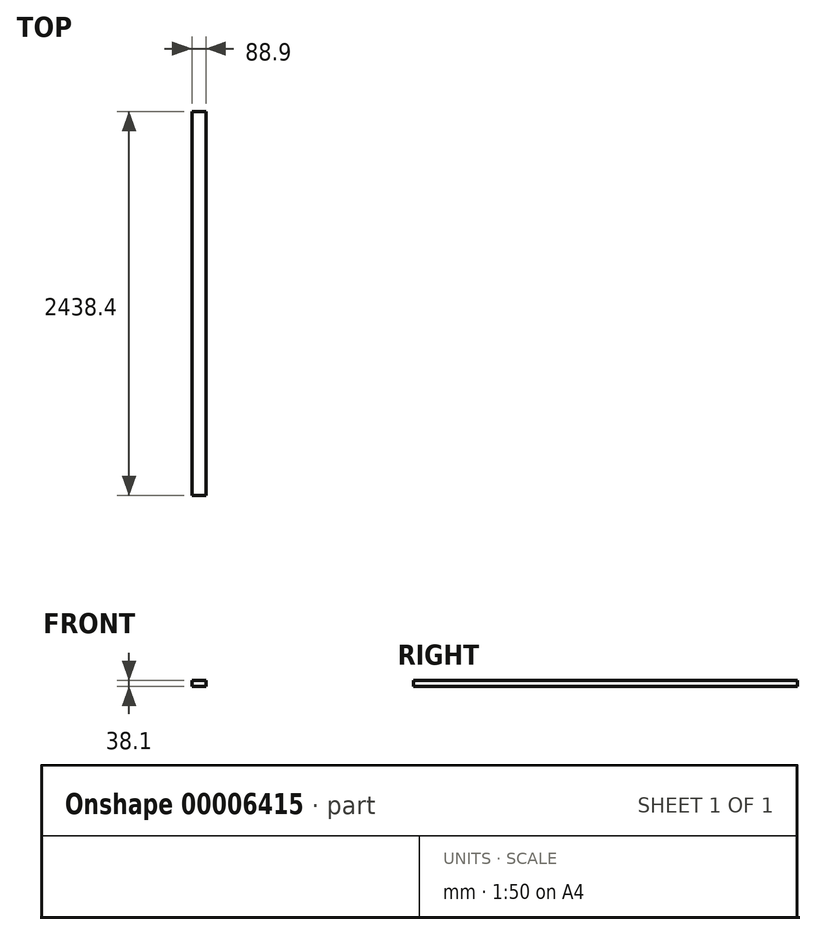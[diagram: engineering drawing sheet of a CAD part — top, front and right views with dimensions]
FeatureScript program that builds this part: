
annotation { "Feature Type Name" : "Feature", "Feature Type Description" : "" }
export const myFeature = defineFeature(function(context is Context, id is Id, definition is map)
    precondition{}
    {
        {
            var Q0;
            Q0=qCreatedBy(makeId("Front.planeOp"),FACE);
            var sketch = newSketch(context, id + "F0", { "sketchPlane" : qUnion([Q0])});
            skLineSegment(sketch, "E0.rect.bottom", {"start": v(44.45, -19.05) * mm, "end": v(-44.45, -19.05) * mm});
            skLineSegment(sketch, "E0.rect.top", {"start": v(44.45, 19.05) * mm, "end": v(-44.45, 19.05) * mm});
            skLineSegment(sketch, "E0.rect.left", {"start": v(44.45, -19.05) * mm, "end": v(44.45, 19.05) * mm});
            skLineSegment(sketch, "E0.rect.right", {"start": v(-44.45, -19.05) * mm, "end": v(-44.45, 19.05) * mm});
            skPoint(sketch, "E0.rect.middle", {"position": v(0, 0) * mm});
            skSolve(sketch);
        }
        {
            var Q0;
            Q0=makeQuery(id+"F0.imprint","IMPRINT",FACE,{"disambiguationData":[TD([[makeQuery(id+"F0.imprint","IMPRINT",EDGE,{"derivedFrom":sQuery(id+"F0.wireOp",EDGE,"E0.rect.bottom")}),-1.0]])]});
            extrude(context, id + "F1", {"entities" : qUnion([Q0]), "depth" : 2438.4 * mm});
        }
    });
